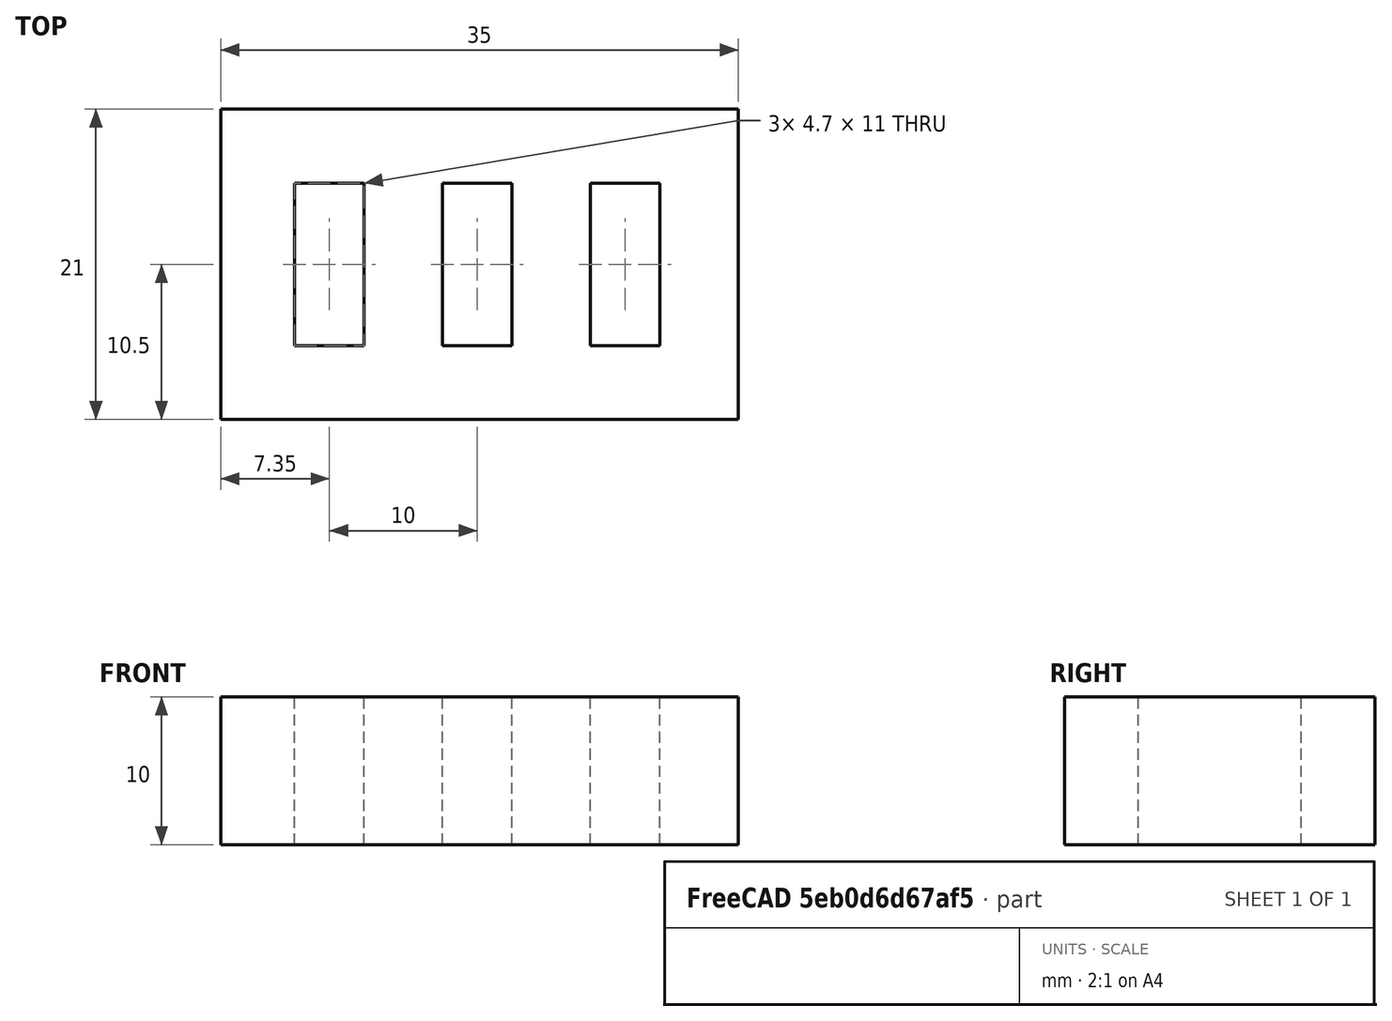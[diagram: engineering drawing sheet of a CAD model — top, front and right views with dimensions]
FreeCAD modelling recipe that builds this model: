
FCSTD DOCUMENT  (FreeCAD 0.20R29177 +426 (Git))
Label: portaPenDrives
License: All rights reserved
LicenseURL: http://en.wikipedia.org/wiki/All_rights_reserved
objects: Part::Box×4, Part::Cut×3
note: 7 computed .brp shape members not serialized (recipe doc carries the construction recipe); baked Part::Feature solids carry a one-line shape summary decoded from their .brp

FEATURE [Part::Box] Box  label="Cubo"
  AttacherType = Attacher::AttachEngine3D
  Height = 10
  Length = 35
  Width = 21
FEATURE [Part::Box] Box001  label="Cubo001"
  AttacherType = Attacher::AttachEngine3D
  Height = 10
  Length = 4.7
  Placement = pos=(5,5,0) rot=(0,0,1;0rad)
  Width = 11
FEATURE [Part::Box] Box002  label="Cubo002"
  AttacherType = Attacher::AttachEngine3D
  Height = 10
  Length = 4.7
  Placement = pos=(15,5,0) rot=(0,0,1;0rad)
  Width = 11
FEATURE [Part::Box] Box003  label="Cubo003"
  AttacherType = Attacher::AttachEngine3D
  Height = 10
  Length = 4.7
  Placement = pos=(25,5,0) rot=(0,0,1;0rad)
  Width = 11
FEATURE [Part::Cut] Cut
  Base = -> Box
  Refine = true
  Tool = -> Box001
FEATURE [Part::Cut] Cut001
  Base = -> Cut
  Refine = true
  Tool = -> Box003
FEATURE [Part::Cut] Cut002
  Base = -> Cut001
  Refine = true
  Tool = -> Box002
